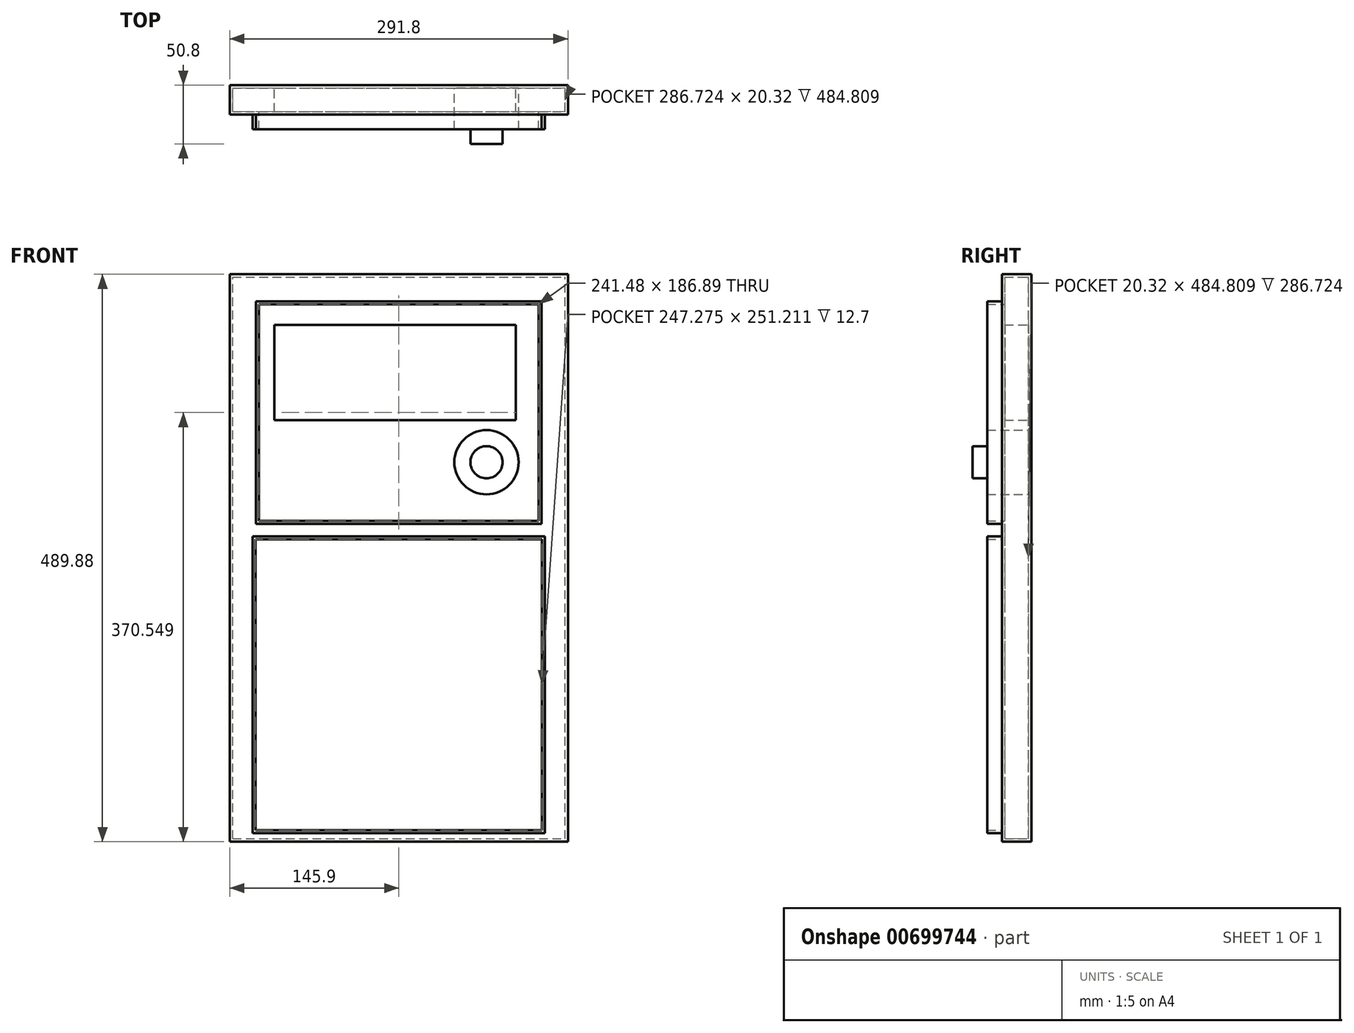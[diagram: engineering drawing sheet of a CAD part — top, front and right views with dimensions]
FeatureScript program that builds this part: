
annotation { "Feature Type Name" : "Feature", "Feature Type Description" : "" }
export const myFeature = defineFeature(function(context is Context, id is Id, definition is map)
    precondition{}
    {
        {
            var Q0;
            Q0=qCreatedBy(makeId("Front.planeOp"),FACE);
            var sketch = newSketch(context, id + "F0", { "sketchPlane" : qUnion([Q0])});
            skLineSegment(sketch, "E0.bottom", {"start": v(-145.9, -244.94) * mm, "end": v(145.9, -244.94) * mm});
            skLineSegment(sketch, "E0.top", {"start": v(-145.9, 244.94) * mm, "end": v(145.9, 244.94) * mm});
            skLineSegment(sketch, "E0.left", {"start": v(-145.9, -244.94) * mm, "end": v(-145.9, 244.94) * mm});
            skLineSegment(sketch, "E0.right", {"start": v(145.9, -244.94) * mm, "end": v(145.9, 244.94) * mm});
            skPoint(sketch, "E0.middle", {"position": v(0, 0) * mm});
            skSolve(sketch);
        }
        {
            var Q0;
            Q0 = qSketchRegion(id + "F0", true);
            extrude(context, id + "F1", {"entities" : qUnion([Q0]), "depth" : 25.4 * mm, "offsetDistance" : 25.4 * mm});
        }
        {
            var Q0;
            Q0=makeQuery(id+"F1.opExtrude","CAP_FACE",FACE,{"disambiguationData":[OSD([sQuery(id+"F0.wireOp",EDGE,"E0.bottom"),sQuery(id+"F0.wireOp",EDGE,"E0.top"),sQuery(id+"F0.wireOp",EDGE,"E0.left"),sQuery(id+"F0.wireOp",EDGE,"E0.right")])],"isStart":false});
            var sketch = newSketch(context, id + "F2", { "sketchPlane" : qUnion([Q0])});
            skLineSegment(sketch, "E1.bottom", {"start": v(-123.28, 29.62) * mm, "end": v(123.28, 29.62) * mm});
            skLineSegment(sketch, "E1.top", {"start": v(-123.28, 221.6) * mm, "end": v(123.28, 221.6) * mm});
            skLineSegment(sketch, "E1.left", {"start": v(-123.28, 29.62) * mm, "end": v(-123.28, 221.6) * mm});
            skLineSegment(sketch, "E1.right", {"start": v(123.28, 29.62) * mm, "end": v(123.28, 221.6) * mm});
            skPoint(sketch, "E1.middle", {"position": v(0, 125.6) * mm});
            skSolve(sketch);
        }
        {
            var Q0;
            Q0=makeQuery(id+"F2.imprint","IMPRINT",FACE,{"disambiguationData":[TD([[makeQuery(id+"F2.imprint","IMPRINT",EDGE,{"derivedFrom":sQuery(id+"F2.wireOp",EDGE,"E1.bottom")}),1.0]])]});
            extrude(context, id + "F3", {"entities" : qUnion([Q0]), "operationType" : NewBodyOperationType.ADD, "depth" : 12.7 * mm, "offsetDistance" : 25.4 * mm});
        }
        {
            var Q0;
            Q0=makeQuery(id+"F3.opExtrude","CAP_FACE",FACE,{"disambiguationData":[OSD([sQuery(id+"F2.wireOp",EDGE,"E1.bottom"),sQuery(id+"F2.wireOp",EDGE,"E1.top"),sQuery(id+"F2.wireOp",EDGE,"E1.left"),sQuery(id+"F2.wireOp",EDGE,"E1.right")])],"isStart":false});
            shell(context, id + "F4", {"entities" : qUnion([Q0]), "thickness" : 2.54 * mm});
        }
        {
            var Q0;
            {var subQ0=sQuery(id+"F0.wireOp",EDGE,"E0.right");var subQ1=sQuery(id+"F0.wireOp",EDGE,"E0.left");var subQ2=sQuery(id+"F0.wireOp",EDGE,"E0.top");var subQ3=sQuery(id+"F0.wireOp",EDGE,"E0.bottom");Q0=makeQuery(id+"F4.opShell","OFFSET_FACE",FACE,{"disambiguationData":[OSD([subQ3,subQ2,subQ1,subQ0]),TDD([makeQuery(id+"F1.opExtrude","CAP_FACE",FACE,{"disambiguationData":[OSD([subQ3,subQ2,subQ1,subQ0])],"isStart":true})])]});}
            var sketch = newSketch(context, id + "F5", { "sketchPlane" : qUnion([Q0])});
            skCircle(sketch, "E2", {"center": v(75.69, 82.7) * mm, "radius": 27.77 * mm});
            skSolve(sketch);
        }
        {
            var Q0;
            Q0=makeQuery(id+"F5.imprint","IMPRINT",FACE,{"disambiguationData":[TD([[makeQuery(id+"F5.imprint","IMPRINT",EDGE,{"derivedFrom":sQuery(id+"F5.wireOp",EDGE,"E2")}),1.0]])]});
            extrude(context, id + "F6", {"entities" : qUnion([Q0]), "operationType" : NewBodyOperationType.ADD, "depth" : 35.56 * mm, "offsetDistance" : 25.4 * mm});
        }
        {
            var Q0;
            Q0=makeQuery(id+"F1.opExtrude","CAP_FACE",FACE,{"disambiguationData":[OSD([sQuery(id+"F0.wireOp",EDGE,"E0.bottom"),sQuery(id+"F0.wireOp",EDGE,"E0.top"),sQuery(id+"F0.wireOp",EDGE,"E0.left"),sQuery(id+"F0.wireOp",EDGE,"E0.right")])],"isStart":false});
            var sketch = newSketch(context, id + "F7", { "sketchPlane" : qUnion([Q0])});
            skLineSegment(sketch, "E3.bottom", {"start": v(-126.18, -237.49) * mm, "end": v(126.18, -237.49) * mm});
            skLineSegment(sketch, "E3.top", {"start": v(-126.18, 18.8) * mm, "end": v(126.18, 18.8) * mm});
            skLineSegment(sketch, "E3.left", {"start": v(-126.18, -237.49) * mm, "end": v(-126.18, 18.8) * mm});
            skLineSegment(sketch, "E3.right", {"start": v(126.18, -237.49) * mm, "end": v(126.18, 18.8) * mm});
            skPoint(sketch, "E3.middle", {"position": v(0, -109.34) * mm});
            skSolve(sketch);
        }
        {
            var Q0;
            Q0=makeQuery(id+"F7.imprint","IMPRINT",FACE,{"disambiguationData":[TD([[makeQuery(id+"F7.imprint","IMPRINT",EDGE,{"derivedFrom":sQuery(id+"F7.wireOp",EDGE,"E3.bottom")}),1.0]])]});
            extrude(context, id + "F8", {"entities" : qUnion([Q0]), "operationType" : NewBodyOperationType.ADD, "depth" : 12.7 * mm, "offsetDistance" : 25.4 * mm});
        }
        {
            var Q0;
            Q0=makeQuery(id+"F8.opExtrude","CAP_FACE",FACE,{"disambiguationData":[OSD([sQuery(id+"F7.wireOp",EDGE,"E3.bottom"),sQuery(id+"F7.wireOp",EDGE,"E3.top"),sQuery(id+"F7.wireOp",EDGE,"E3.left"),sQuery(id+"F7.wireOp",EDGE,"E3.right")])],"isStart":false});
            shell(context, id + "F9", {"entities" : qUnion([Q0]), "thickness" : 2.54 * mm});
        }
        {
            var Q0;
            {var subQ0=sQuery(id+"F0.wireOp",EDGE,"E0.right");var subQ1=sQuery(id+"F0.wireOp",EDGE,"E0.left");var subQ2=sQuery(id+"F0.wireOp",EDGE,"E0.top");var subQ3=sQuery(id+"F0.wireOp",EDGE,"E0.bottom");Q0=makeQuery(id+"F4.opShell","OFFSET_FACE",FACE,{"disambiguationData":[OSD([subQ3,subQ2,subQ1,subQ0]),TDD([makeQuery(id+"F1.opExtrude","CAP_FACE",FACE,{"disambiguationData":[OSD([subQ3,subQ2,subQ1,subQ0])],"isStart":true})])]});}
            var sketch = newSketch(context, id + "F10", { "sketchPlane" : qUnion([Q0])});
            skLineSegment(sketch, "E4.bottom", {"start": v(-107.47, 201.2) * mm, "end": v(100.82, 201.2) * mm});
            skLineSegment(sketch, "E4.top", {"start": v(-107.47, 119.14) * mm, "end": v(100.82, 119.14) * mm});
            skLineSegment(sketch, "E4.left", {"start": v(-107.47, 201.2) * mm, "end": v(-107.47, 119.14) * mm});
            skLineSegment(sketch, "E4.right", {"start": v(100.82, 201.2) * mm, "end": v(100.82, 119.14) * mm});
            skSolve(sketch);
        }
        {
            var Q0;
            Q0=makeQuery(id+"F10.imprint","IMPRINT",FACE,{"disambiguationData":[TD([[makeQuery(id+"F10.imprint","IMPRINT",EDGE,{"derivedFrom":sQuery(id+"F10.wireOp",EDGE,"E4.bottom")}),-1.0]])]});
            extrude(context, id + "F11", {"entities" : qUnion([Q0]), "operationType" : NewBodyOperationType.ADD, "depth" : 20.32 * mm, "offsetDistance" : 25.4 * mm});
        }
        {
            var Q0;
            Q0=makeQuery(id+"F6.opExtrude","CAP_FACE",FACE,{"disambiguationData":[OSD([sQuery(id+"F5.wireOp",EDGE,"E2")])],"isStart":false});
            var sketch = newSketch(context, id + "F12", { "sketchPlane" : qUnion([Q0])});
            skCircle(sketch, "E5", {"center": v(75.69, 82.7) * mm, "radius": 13.93 * mm});
            skSolve(sketch);
        }
        {
            var Q0;
            Q0=makeQuery(id+"F12.imprint","IMPRINT",FACE,{"disambiguationData":[TD([[makeQuery(id+"F12.imprint","IMPRINT",EDGE,{"derivedFrom":sQuery(id+"F12.wireOp",EDGE,"E5")}),1.0]])]});
            extrude(context, id + "F13", {"entities" : qUnion([Q0]), "operationType" : NewBodyOperationType.ADD, "depth" : 12.7 * mm, "offsetDistance" : 25.4 * mm});
        }
    });
